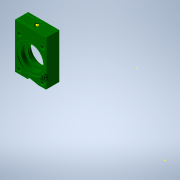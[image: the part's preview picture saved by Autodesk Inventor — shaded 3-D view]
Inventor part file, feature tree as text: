
AUTODESK INVENTOR PART (.ipt)
format: ipt  version: 2020 (Build 240168000, 168)  size: 570,368 bytes
history: native  units: in
note: dims shown in document units (in); Inventor stores cm internally (conversion verified against a paired STEP export)
features: hole x6, sketch x5, extrude x4, fillet x1
ambient origin geometry x8: Origin, YZ Plane, XZ Plane, XY Plane, X Axis, Y Axis, Z Axis, Center Point
bodies: Solid1 (feature_tree)
feature tree (16):
  extrude  "Extrusion1"  Depth=0.4in TaperAngle=0.0deg
  extrude  "Extrusion2"  Depth=0.25in
  sketch  "Sketch3"  dims[d6=0.213in d7=0.75in d8=0.507in d9=0.25in d10=0.5635in d11=0.25in d12=0.0in]
  extrude  "Extrusion3"  Depth=0.0312in
  hole  "Hole1"  [1 undecoded]
  hole  "Hole2"  [1 undecoded]
  extrude  "Extrusion4"  Depth=0.0312in
  hole  "Hole5"  [1 undecoded]
  hole  "Hole6"  [1 undecoded]
  fillet  "Fillet1"  Radius=0.314in
  sketch  "Sketch4"  dims[d13=0.04in d14=0.75in d15=0.507in d16=0.25in d17=0.5635in d18=1.0in d19=0.8108in d20=0.4583in]
  hole  "Hole3"  [1 undecoded]
  hole  "Hole4"  [1 undecoded]
  sketch  "Sketch1"  dims[d0=0.4in d1=0.0in d2=0.4in d3=0.0in]
  sketch  "Sketch2"  dims[d4=0.6in d5=0.0in]
  sketch  "Sketch5"  dims[d21=0.29in d22=0.04in d23=0.75in d24=0.507in d25=0.25in d26=0.5635in d27=1.0in d28=0.8108in d29=0.213in d30=0.75in d31=0.507in d32=0.25in d33=0.5635in d34=0.25in d35=0.0in d36=0.75in d38=135.0deg d39=0.4583in d40=0.6957in d41=0.25in d42=1.0in d43=0.0in d44=0.314in d45=0.221in d46=0.213in d47=0.75in d48=0.375in d49=0.25in d50=0.5635in d51=0.25in d52=0.0in d53=0.04in d54=0.75in d55=0.375in d56=0.25in d57=0.5635in d58=0.75in d59=0.8108in d60=0.0312in d61=1.1595in d62=0.221in]
note: 6 required parameter values undecoded (feature->parameter linkage not recoverable at this tier; creation-order binding heuristic only, values carry confidence <= 0.55)
